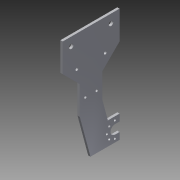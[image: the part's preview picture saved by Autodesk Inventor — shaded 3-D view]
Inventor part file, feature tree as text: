
AUTODESK INVENTOR PART (.ipt)
format: ipt  version: 2013 (Build 170138000, 138)  size: 172,544 bytes
history: native  units: mm
features: sketch x5, extrude x3, hole x2, other x1, pattern_circular x1
ambient origin geometry x8: Origin, YZ Plane, XZ Plane, XY Plane, X Axis, Y Axis, Z Axis, Center Point
feature tree (12):
  other  "ソリッド1"
  extrude  "押し出し1"  Depth=50.0mm
  extrude  "押し出し2"  Depth=100.0mm
  extrude  "押し出し5"  Depth=50.0mm
  hole  "穴1"  [1 undecoded]
  pattern_circular  "円形状パターン2"  [2 undecoded]
  hole  "穴2"  [1 undecoded]
  sketch  "スケッチ1"
  sketch  "スケッチ2"
  sketch  "スケッチ3"
  sketch  "スケッチ4"
  sketch  "スケッチ5"
note: 4 required parameter values undecoded (feature->parameter linkage not recoverable at this tier; creation-order binding heuristic only, values carry confidence <= 0.55)
